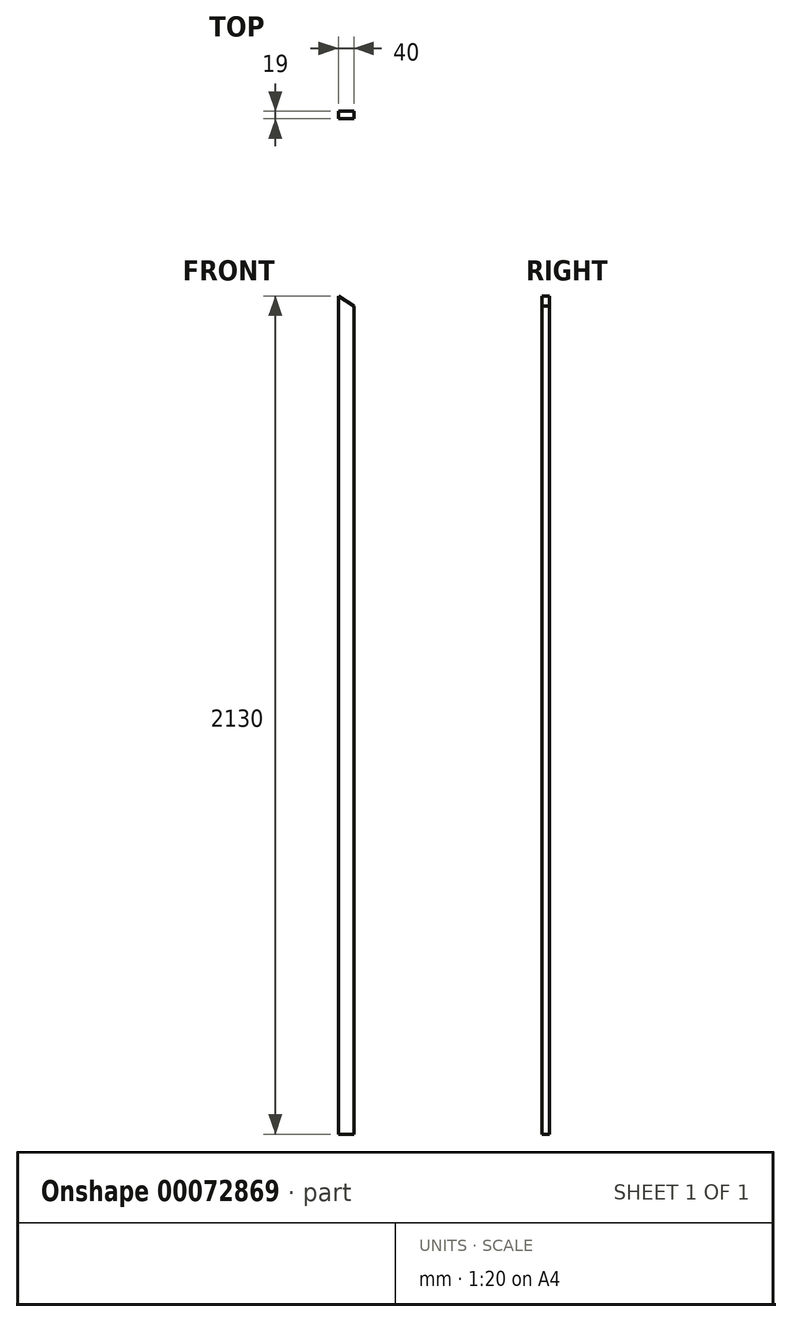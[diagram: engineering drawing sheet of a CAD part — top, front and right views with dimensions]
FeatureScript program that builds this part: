
annotation { "Feature Type Name" : "Feature", "Feature Type Description" : "" }
export const myFeature = defineFeature(function(context is Context, id is Id, definition is map)
    precondition{}
    {
        {
            var Q0;
            Q0=qCreatedBy(makeId("Front.planeOp"),FACE);
            var sketch = newSketch(context, id + "F0", { "sketchPlane" : qUnion([Q0])});
            skLineSegment(sketch, "E0.top", {"start": v(0, -2130) * mm, "end": v(40, -2130) * mm});
            skLineSegment(sketch, "E0.left", {"start": v(0, 0) * mm, "end": v(0, -2130) * mm});
            skLineSegment(sketch, "E0.right", {"start": v(40, -25.3) * mm, "end": v(40, -2130) * mm});
            skLineSegment(sketch, "E1", {"start": v(0, 0) * mm, "end": v(40, -25.3) * mm});
            skSolve(sketch);
        }
        {
            var Q0;
            Q0=makeQuery(id+"F0.imprint","IMPRINT",FACE,{"disambiguationData":[TD([[makeQuery(id+"F0.imprint","IMPRINT",EDGE,{"derivedFrom":sQuery(id+"F0.wireOp",EDGE,"E0.top")}),1.0]])]});
            extrude(context, id + "F1", {"entities" : qUnion([Q0]), "depth" : 19 * mm});
        }
    });
